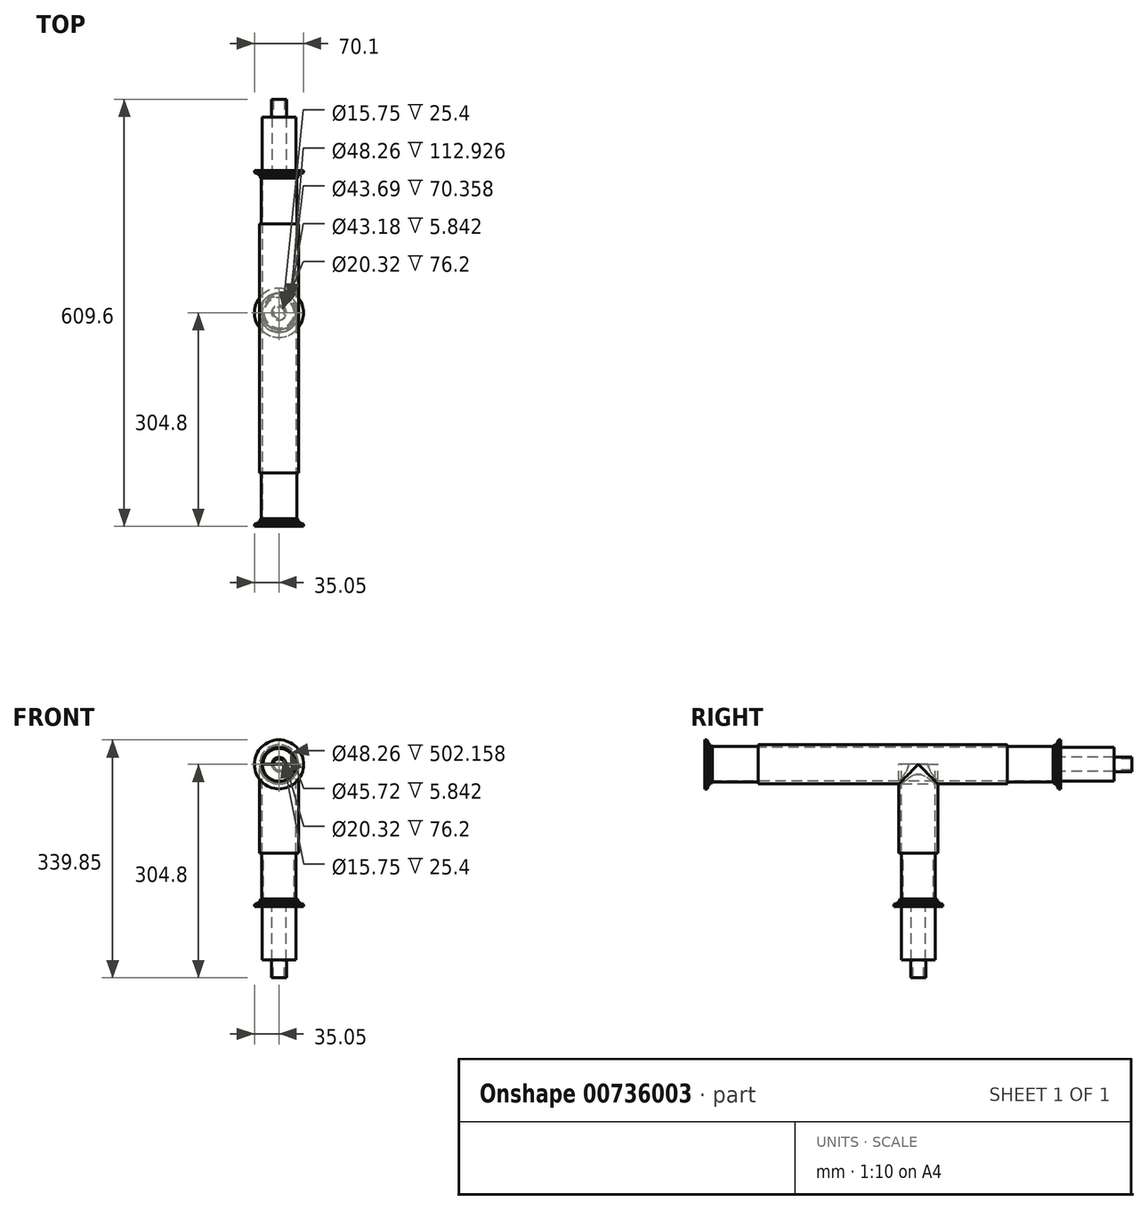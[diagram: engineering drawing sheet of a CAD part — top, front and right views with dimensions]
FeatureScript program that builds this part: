
annotation { "Feature Type Name" : "Feature", "Feature Type Description" : "" }
export const myFeature = defineFeature(function(context is Context, id is Id, definition is map)
    precondition{}
    {
        {
            var Q0;
            Q0=qCreatedBy(makeId("Front.planeOp"),FACE);
            var sketch = newSketch(context, id + "F0", { "sketchPlane" : qUnion([Q0])});
            skCircle(sketch, "E0", {"center": v(0, 0) * mm, "radius": 22.23 * mm, "construction": true});
            skSolve(sketch);
        }
        {
            var Q0;
            Q0=qCreatedBy(makeId("Front.planeOp"),FACE);
            var sketch = newSketch(context, id + "F1", { "sketchPlane" : qUnion([Q0])});
            skCircle(sketch, "E1", {"center": v(0, 0) * mm, "radius": 24.13 * mm});
            skCircle(sketch, "E2", {"center": v(0, 0) * mm, "radius": 35.05 * mm});
            skSolve(sketch);
        }
        {
            var Q0;
            Q0=qSketchRegion(id+"F1",true);
            extrude(context, id + "F2", {"entities" : qUnion([Q0]), "oppositeDirection" : true, "depth" : 5.84 * mm, "offsetDistance" : 25.4 * mm});
        }
        {
            var Q0;
            Q0=makeQuery(id+"F2.opExtrude","CAP_EDGE",EDGE,{"disambiguationData":[OSD([sQuery(id+"F1.wireOp",EDGE,"E2")])],"isStart":false});
            chamfer(context, id + "F3", {"entities" : qUnion([Q0]), "chamferType" : ChamferType.OFFSET_ANGLE, "width" : 2.54 * mm, "oppositeDirection" : false, "angle" : 70 * degree, "tangentPropagation" : true});
        }
        {
            var Q0;
            Q0=makeQuery(id+"F2.opExtrude","CAP_FACE",FACE,{"disambiguationData":[OSD([sQuery(id+"F1.wireOp",EDGE,"E1"),sQuery(id+"F1.wireOp",EDGE,"E2")])],"isStart":false});
            var sketch = newSketch(context, id + "F4", { "sketchPlane" : qUnion([Q0])});
            skCircle(sketch, "E3", {"center": v(0, 0) * mm, "radius": 28.07 * mm});
            skCircle(sketch, "E4", {"center": v(0, 0) * mm, "radius": 24.13 * mm});
            skSolve(sketch);
        }
        {
            var Q0;
            Q0=qSketchRegion(id+"F4",true);
            extrude(context, id + "F5", {"entities" : qUnion([Q0]), "operationType" : NewBodyOperationType.ADD, "depth" : 2.54 * mm, "offsetDistance" : 25.4 * mm});
        }
        {
            var Q0;
            Q0=makeQuery(id+"F5.opExtrude","CAP_FACE",FACE,{"disambiguationData":[OSD([sQuery(id+"F4.wireOp",EDGE,"E3"),sQuery(id+"F4.wireOp",EDGE,"E4")])],"isStart":false});
            var sketch = newSketch(context, id + "F6", { "sketchPlane" : qUnion([Q0])});
            skCircle(sketch, "E5", {"center": v(0, 0) * mm, "radius": 26.55 * mm});
            skCircle(sketch, "E6", {"center": v(0, 0) * mm, "radius": 24.13 * mm});
            skSolve(sketch);
        }
        {
            var Q0;
            Q0=qSketchRegion(id+"F6",true);
            extrude(context, id + "F7", {"entities" : qUnion([Q0]), "operationType" : NewBodyOperationType.ADD, "depth" : 2.54 * mm, "offsetDistance" : 25.4 * mm});
        }
        {
            var Q0;
            Q0=makeQuery(id+"F7.opExtrude","CAP_FACE",FACE,{"disambiguationData":[OSD([sQuery(id+"F6.wireOp",EDGE,"E5"),sQuery(id+"F6.wireOp",EDGE,"E6")])],"isStart":false});
            var sketch = newSketch(context, id + "F8", { "sketchPlane" : qUnion([Q0])});
            skCircle(sketch, "E7", {"center": v(0, 0) * mm, "radius": 24.13 * mm});
            skCircle(sketch, "E8", {"center": v(0, 0) * mm, "radius": 25.4 * mm});
            skSolve(sketch);
        }
        {
            var Q0;
            Q0=qSketchRegion(id+"F8",true);
            extrude(context, id + "F9", {"entities" : qUnion([Q0]), "operationType" : NewBodyOperationType.ADD, "depth" : 65.28 * mm, "offsetDistance" : 25.4 * mm});
        }
        {
            var Q0;
            Q0=makeQuery(id+"F9.opExtrude","CAP_FACE",FACE,{"disambiguationData":[OSD([sQuery(id+"F8.wireOp",EDGE,"E7"),sQuery(id+"F8.wireOp",EDGE,"E8")])],"isStart":false});
            var sketch = newSketch(context, id + "F10", { "sketchPlane" : qUnion([Q0])});
            skCircle(sketch, "E9", {"center": v(0, 0) * mm, "radius": 27.94 * mm});
            skCircle(sketch, "E10", {"center": v(0, 0) * mm, "radius": 24.13 * mm});
            skSolve(sketch);
        }
        {
            var Q0;
            Q0=qCreatedBy(makeId("Right.planeOp"),FACE);
            var sketch = newSketch(context, id + "F11", { "sketchPlane" : qUnion([Q0])});
            skLineSegment(sketch, "E11", {"start": v(76.2, 0) * mm, "end": v(431.8, 0) * mm});
            skSolve(sketch);
        }
        {
            var Q0;
            Q0=qSketchRegion(id+"F10",true);
            var Q1;
            Q1=qConstructionFilter(qBodyType(qCreatedBy(id+"F11",EDGE),BodyType.WIRE),ConstructionObject.NO);
            sweep(context, id + "F12", {"operationType" : NewBodyOperationType.ADD, "profiles" : qUnion([Q0]), "path" : qUnion([Q1])});
        }
        {
            var Q0;
            Q0=makeQuery(id+"F12.opSweep","CAP_FACE",FACE,{"disambiguationData":[OSD([sQuery(id+"F10.wireOp",EDGE,"E9"),sQuery(id+"F10.wireOp",EDGE,"E10"),sQuery(id+"F11.wireOp",VERTEX,"7ykRA0Qg-2DrY-rTCa-7tXY-ZQoEE0Xzwcjr.end")])],"isStart":false});
            var sketch = newSketch(context, id + "F13", { "sketchPlane" : qUnion([Q0])});
            skCircle(sketch, "E12", {"center": v(0, 0) * mm, "radius": 24.13 * mm});
            skCircle(sketch, "E13", {"center": v(0, 0) * mm, "radius": 25.4 * mm});
            skSolve(sketch);
        }
        {
            var Q0;
            Q0=makeQuery(id+"F12.opSweep","CAP_EDGE",EDGE,{"disambiguationData":[OSD([sQuery(id+"F10.wireOp",EDGE,"E9"),sQuery(id+"F11.wireOp",VERTEX,"7ykRA0Qg-2DrY-rTCa-7tXY-ZQoEE0Xzwcjr.end")])],"isStart":false});
            fillet(context, id + "F14", {"entities" : qUnion([Q0]), "radius" : 1.27 * mm, "tangentPropagation" : true, "allowEdgeOverflow" : false});
        }
        {
            var Q0;
            Q0=qSketchRegion(id+"F13",true);
            extrude(context, id + "F15", {"entities" : qUnion([Q0]), "operationType" : NewBodyOperationType.ADD, "depth" : 76.2 * mm, "offsetDistance" : 25.4 * mm});
        }
        {
            var Q0;
            Q0=makeQuery(id+"F15.opExtrude","CAP_FACE",FACE,{"disambiguationData":[OSD([sQuery(id+"F13.wireOp",EDGE,"E12"),sQuery(id+"F13.wireOp",EDGE,"E13")])],"isStart":false});
            var sketch = newSketch(context, id + "F16", { "sketchPlane" : qUnion([Q0])});
            skCircle(sketch, "E14", {"center": v(0, 0) * mm, "radius": 35.05 * mm});
            skCircle(sketch, "E15", {"center": v(0, 0) * mm, "radius": 22.86 * mm});
            skSolve(sketch);
        }
        {
            var Q0;
            Q0=qSketchRegion(id+"F16",true);
            extrude(context, id + "F17", {"entities" : qUnion([Q0]), "operationType" : NewBodyOperationType.ADD, "oppositeDirection" : true, "depth" : 5.84 * mm, "offsetDistance" : 25.4 * mm});
        }
        {
            var Q0;
            Q0=makeQuery(id+"F17.opExtrude","CAP_EDGE",EDGE,{"disambiguationData":[OSD([sQuery(id+"F16.wireOp",EDGE,"E14")])],"isStart":false});
            chamfer(context, id + "F18", {"entities" : qUnion([Q0]), "chamferType" : ChamferType.OFFSET_ANGLE, "width" : 2.54 * mm, "oppositeDirection" : false, "angle" : 70 * degree, "tangentPropagation" : true});
        }
        {
            var Q0;
            Q0=makeQuery(id+"F17.opExtrude","CAP_FACE",FACE,{"disambiguationData":[OSD([sQuery(id+"F16.wireOp",EDGE,"E14"),sQuery(id+"F16.wireOp",EDGE,"E15")])],"isStart":false});
            var sketch = newSketch(context, id + "F19", { "sketchPlane" : qUnion([Q0])});
            skCircle(sketch, "E16", {"center": v(0, 0) * mm, "radius": 24.13 * mm});
            skCircle(sketch, "E17", {"center": v(0, 0) * mm, "radius": 28.07 * mm});
            skSolve(sketch);
        }
        {
            var Q0;
            Q0=qSketchRegion(id+"F19",true);
            extrude(context, id + "F20", {"entities" : qUnion([Q0]), "operationType" : NewBodyOperationType.ADD, "depth" : 2.54 * mm, "offsetDistance" : 25.4 * mm});
        }
        {
            var Q0;
            Q0=makeQuery(id+"F20.opExtrude","CAP_FACE",FACE,{"disambiguationData":[OSD([sQuery(id+"F19.wireOp",EDGE,"E16"),sQuery(id+"F19.wireOp",EDGE,"E17")])],"isStart":false});
            var sketch = newSketch(context, id + "F21", { "sketchPlane" : qUnion([Q0])});
            skCircle(sketch, "E18", {"center": v(0, 0) * mm, "radius": 24.13 * mm});
            skCircle(sketch, "E19", {"center": v(0, 0) * mm, "radius": 26.8 * mm});
            skSolve(sketch);
        }
        {
            var Q0;
            Q0=qSketchRegion(id+"F21",true);
            extrude(context, id + "F22", {"entities" : qUnion([Q0]), "operationType" : NewBodyOperationType.ADD, "depth" : 2.54 * mm, "offsetDistance" : 25.4 * mm});
        }
        {
            var Q0;
            Q0=makeQuery(id+"F17.boolean.opBoolean","MERGE",FACE,{"derivedFrom":[makeQuery(id+"F15.opExtrude","CAP_FACE",FACE,{"disambiguationData":[OSD([sQuery(id+"F13.wireOp",EDGE,"E12"),sQuery(id+"F13.wireOp",EDGE,"E13")])],"isStart":false}),makeQuery(id+"F17.opExtrude","CAP_FACE",FACE,{"disambiguationData":[OSD([sQuery(id+"F16.wireOp",EDGE,"E14"),sQuery(id+"F16.wireOp",EDGE,"E15")])],"isStart":true})]});
            var sketch = newSketch(context, id + "F23", { "sketchPlane" : qUnion([Q0])});
            skCircle(sketch, "E20", {"center": v(0, 0) * mm, "radius": 10.16 * mm});
            skCircle(sketch, "E21", {"center": v(0, 0) * mm, "radius": 24.13 * mm});
            skSolve(sketch);
        }
        {
            var Q0;
            Q0=qSketchRegion(id+"F23",true);
            extrude(context, id + "F24", {"entities" : qUnion([Q0]), "operationType" : NewBodyOperationType.ADD, "depth" : 76.2 * mm, "offsetDistance" : 25.4 * mm});
        }
        {
            var Q0;
            Q0=makeQuery(id+"F24.opExtrude","CAP_FACE",FACE,{"disambiguationData":[OSD([sQuery(id+"F23.wireOp",EDGE,"E20"),sQuery(id+"F23.wireOp",EDGE,"E21")])],"isStart":false});
            var sketch = newSketch(context, id + "F25", { "sketchPlane" : qUnion([Q0])});
            skCircle(sketch, "E22", {"center": v(0, 0) * mm, "radius": 10.67 * mm});
            skCircle(sketch, "E23", {"center": v(0, 0) * mm, "radius": 7.87 * mm});
            skSolve(sketch);
        }
        {
            var Q0;
            Q0=qSketchRegion(id+"F25",true);
            extrude(context, id + "F26", {"entities" : qUnion([Q0]), "operationType" : NewBodyOperationType.ADD, "depth" : 25.4 * mm, "offsetDistance" : 25.4 * mm});
        }
        {
            var Q0;
            Q0=qCreatedBy(makeId("Right.planeOp"),FACE);
            var sketch = newSketch(context, id + "F27", { "sketchPlane" : qUnion([Q0])});
            skLineSegment(sketch, "E24", {"start": v(0, 0) * mm, "end": v(609.6, 0) * mm});
            skSolve(sketch);
        }
        {
            var Q0;
            Q0=qCreatedBy(makeId("Top.planeOp"),FACE);
            var sketch = newSketch(context, id + "F28", { "sketchPlane" : qUnion([Q0])});
            skCircle(sketch, "E25", {"center": v(0, 304.8) * mm, "radius": 27.94 * mm});
            skCircle(sketch, "E26", {"center": v(0, 304.8) * mm, "radius": 24.13 * mm});
            skSolve(sketch);
        }
        {
            var Q0;
            Q0=qSketchRegion(id+"F28",true);
            extrude(context, id + "F29", {"entities" : qUnion([Q0]), "operationType" : NewBodyOperationType.ADD, "oppositeDirection" : true, "depth" : 127 * mm, "offsetDistance" : 25.4 * mm});
        }
        {
            var Q0;
            Q0=makeQuery(id+"F29.opExtrude","CAP_FACE",FACE,{"disambiguationData":[OSD([sQuery(id+"F28.wireOp",EDGE,"E25"),sQuery(id+"F28.wireOp",EDGE,"E26")])],"isStart":false});
            var sketch = newSketch(context, id + "F30", { "sketchPlane" : qUnion([Q0])});
            skCircle(sketch, "E27", {"center": v(0, -304.8) * mm, "radius": 24.38 * mm});
            skCircle(sketch, "E28", {"center": v(0, -304.8) * mm, "radius": 21.84 * mm});
            skSolve(sketch);
        }
        {
            var Q0;
            Q0=qSketchRegion(id+"F30",true);
            extrude(context, id + "F31", {"entities" : qUnion([Q0]), "operationType" : NewBodyOperationType.ADD, "depth" : 76.2 * mm, "offsetDistance" : 25.4 * mm});
        }
        {
            var Q0;
            Q0=makeQuery(id+"F31.opExtrude","CAP_FACE",FACE,{"disambiguationData":[OSD([sQuery(id+"F30.wireOp",EDGE,"E27"),sQuery(id+"F30.wireOp",EDGE,"E28")])],"isStart":false});
            var sketch = newSketch(context, id + "F32", { "sketchPlane" : qUnion([Q0])});
            skCircle(sketch, "E29", {"center": v(0, -304.8) * mm, "radius": 21.59 * mm});
            skCircle(sketch, "E30", {"center": v(0, -304.8) * mm, "radius": 35.05 * mm});
            skSolve(sketch);
        }
        {
            var Q0;
            Q0=qSketchRegion(id+"F32",true);
            extrude(context, id + "F33", {"entities" : qUnion([Q0]), "operationType" : NewBodyOperationType.ADD, "oppositeDirection" : true, "depth" : 5.84 * mm, "offsetDistance" : 25.4 * mm});
        }
        {
            var Q0;
            Q0=makeQuery(id+"F33.opExtrude","CAP_EDGE",EDGE,{"disambiguationData":[OSD([sQuery(id+"F32.wireOp",EDGE,"E30")])],"isStart":false});
            chamfer(context, id + "F34", {"entities" : qUnion([Q0]), "chamferType" : ChamferType.OFFSET_ANGLE, "width" : 2.54 * mm, "oppositeDirection" : false, "angle" : 70 * degree, "tangentPropagation" : true});
        }
        {
            var Q0;
            Q0=makeQuery(id+"F33.opExtrude","CAP_FACE",FACE,{"disambiguationData":[OSD([sQuery(id+"F32.wireOp",EDGE,"E29"),sQuery(id+"F32.wireOp",EDGE,"E30")])],"isStart":false});
            var sketch = newSketch(context, id + "F35", { "sketchPlane" : qUnion([Q0])});
            skCircle(sketch, "E31", {"center": v(0, 304.8) * mm, "radius": 28.07 * mm});
            skCircle(sketch, "E32", {"center": v(0, 304.8) * mm, "radius": 24.38 * mm});
            skSolve(sketch);
        }
        {
            var Q0;
            Q0=qSketchRegion(id+"F35",true);
            extrude(context, id + "F36", {"entities" : qUnion([Q0]), "operationType" : NewBodyOperationType.ADD, "depth" : 2.54 * mm, "offsetDistance" : 25.4 * mm});
        }
        {
            var Q0;
            Q0=makeQuery(id+"F36.opExtrude","CAP_FACE",FACE,{"disambiguationData":[OSD([sQuery(id+"F35.wireOp",EDGE,"E31"),sQuery(id+"F35.wireOp",EDGE,"E32")])],"isStart":false});
            var sketch = newSketch(context, id + "F37", { "sketchPlane" : qUnion([Q0])});
            skCircle(sketch, "E33", {"center": v(0, 304.8) * mm, "radius": 26.8 * mm});
            skCircle(sketch, "E34", {"center": v(0, 304.8) * mm, "radius": 24.38 * mm});
            skSolve(sketch);
        }
        {
            var Q0;
            Q0=qSketchRegion(id+"F37",true);
            extrude(context, id + "F38", {"entities" : qUnion([Q0]), "operationType" : NewBodyOperationType.ADD, "depth" : 2.54 * mm, "offsetDistance" : 25.4 * mm});
        }
        {
            var Q0;
            Q0=makeQuery(id+"F33.boolean.opBoolean","MERGE",FACE,{"derivedFrom":[makeQuery(id+"F31.opExtrude","CAP_FACE",FACE,{"disambiguationData":[OSD([sQuery(id+"F30.wireOp",EDGE,"E27"),sQuery(id+"F30.wireOp",EDGE,"E28")])],"isStart":false}),makeQuery(id+"F33.opExtrude","CAP_FACE",FACE,{"disambiguationData":[OSD([sQuery(id+"F32.wireOp",EDGE,"E29"),sQuery(id+"F32.wireOp",EDGE,"E30")])],"isStart":true})]});
            var sketch = newSketch(context, id + "F39", { "sketchPlane" : qUnion([Q0])});
            skCircle(sketch, "E35", {"center": v(0, -304.8) * mm, "radius": 10.16 * mm});
            skCircle(sketch, "E36", {"center": v(0, -304.8) * mm, "radius": 24.13 * mm});
            skSolve(sketch);
        }
        {
            var Q0;
            Q0=qSketchRegion(id+"F39",true);
            extrude(context, id + "F40", {"entities" : qUnion([Q0]), "operationType" : NewBodyOperationType.ADD, "depth" : 76.2 * mm, "offsetDistance" : 25.4 * mm});
        }
        {
            var Q0;
            Q0=makeQuery(id+"F40.opExtrude","CAP_FACE",FACE,{"disambiguationData":[OSD([sQuery(id+"F39.wireOp",EDGE,"E35"),sQuery(id+"F39.wireOp",EDGE,"E36")])],"isStart":false});
            var sketch = newSketch(context, id + "F41", { "sketchPlane" : qUnion([Q0])});
            skCircle(sketch, "E37", {"center": v(0, -304.8) * mm, "radius": 10.67 * mm});
            skCircle(sketch, "E38", {"center": v(0, -304.8) * mm, "radius": 7.87 * mm});
            skSolve(sketch);
        }
        {
            var Q0;
            Q0=qSketchRegion(id+"F41",true);
            extrude(context, id + "F42", {"entities" : qUnion([Q0]), "operationType" : NewBodyOperationType.ADD, "depth" : 25.4 * mm, "offsetDistance" : 25.4 * mm});
        }
    });
